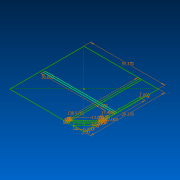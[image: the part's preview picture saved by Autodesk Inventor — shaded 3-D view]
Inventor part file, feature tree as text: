
AUTODESK INVENTOR PART (.ipt)
format: ipt  version: 2022.2 (Build 262287000, 287)  size: 106,496 bytes
history: native  units: in
note: dims shown in document units (in); Inventor stores cm internally (conversion verified against a paired STEP export)
features: sketch x1
ambient origin geometry x8: Origin, YZ Plane, XZ Plane, XY Plane, X Axis, Y Axis, Z Axis, Center Point
feature tree (1):
  sketch  "Sketch1"  dims[d4=1.5in d7=39.3701in d8=39.3701in d27=45.0deg d31=1.0in d32=1.0in d34=0.5in d35=0.5in d36=0.5in d37=0.5in d38=0.5in d39=0.5in d40=0.5in d41=0.5in d45=38.9706in d46=0.25in d48=8.0in d51=0.25in d52=0.25in d53=13.0in d54=22.0in d55=1.0in d56=7.4853in d58=38.0in]
